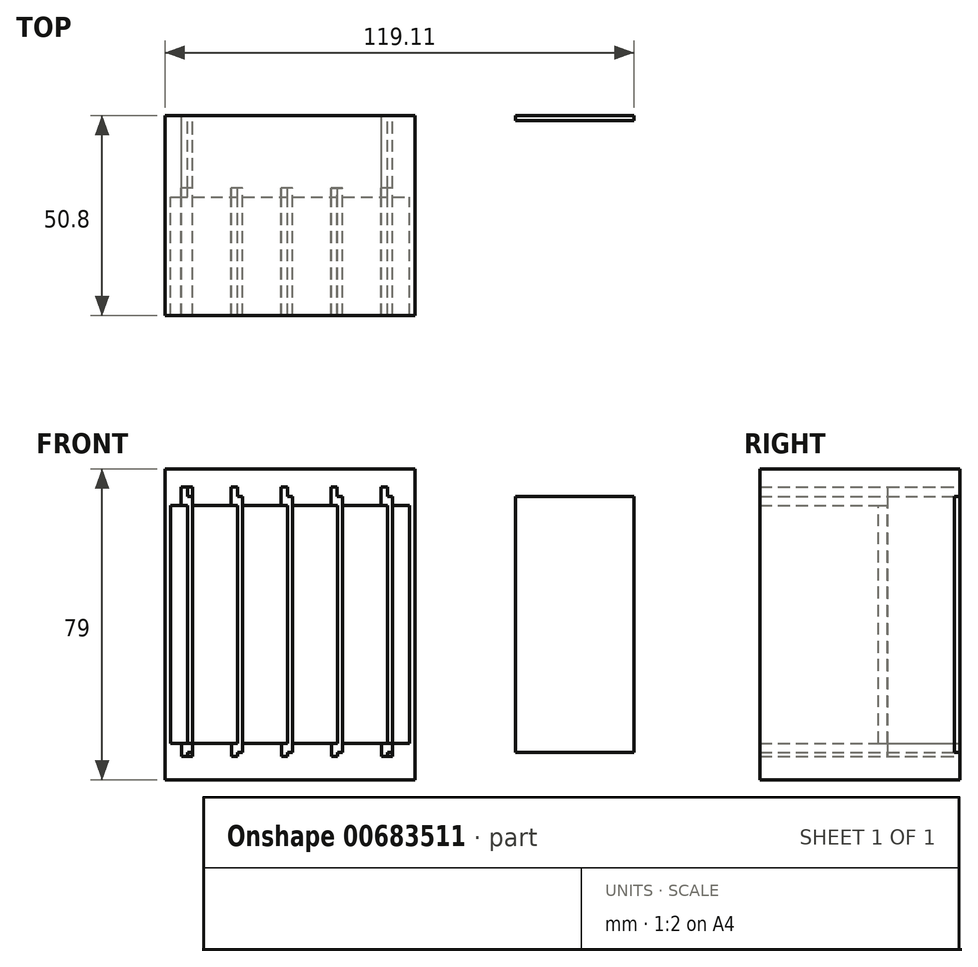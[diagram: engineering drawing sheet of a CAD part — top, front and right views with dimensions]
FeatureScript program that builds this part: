
annotation { "Feature Type Name" : "Feature", "Feature Type Description" : "" }
export const myFeature = defineFeature(function(context is Context, id is Id, definition is map)
    precondition{}
    {
        {
            var Q0;
            Q0=qCreatedBy(makeId("Front.planeOp"),FACE);
            var sketch = newSketch(context, id + "F0", { "sketchPlane" : qUnion([Q0])});
            skPoint(sketch, "E0.middle", {"position": v(-26.63, 1.14) * mm});
            skPoint(sketch, "E0.middle.positionSnap0", {"position": v(-32.98, 1.14) * mm});
            skPoint(sketch, "E0.centerSnap0", {"position": v(-32.98, 1.14) * mm});
            skLineSegment(sketch, "E1", {"start": v(30.52, 31.34) * mm, "end": v(30.52, -30.2) * mm});
            skPoint(sketch, "E2.middle", {"position": v(-13.93, 0) * mm});
            skPoint(sketch, "E3.middle", {"position": v(-1.23, 0) * mm});
            skPoint(sketch, "E4.middle", {"position": v(11.47, 0) * mm});
            skPoint(sketch, "E5.MirrorP", {"position": v(-61.95, 0) * mm});
            skLineSegment(sketch, "E6.MirrorCS", {"start": v(29.13, 32.48) * mm, "end": v(29.13, -30.2) * mm});
            skLineSegment(sketch, "E7.top", {"start": v(23.5, 31.34) * mm, "end": v(24.83, 31.34) * mm});
            skLineSegment(sketch, "E7.left", {"start": v(23.5, -30.2) * mm, "end": v(23.5, 31.34) * mm});
            skLineSegment(sketch, "E7.right", {"start": v(24.83, -30.2) * mm, "end": v(24.83, 31.34) * mm});
            skLineSegment(sketch, "E8.top", {"start": v(10.8, 31.34) * mm, "end": v(12.13, 31.34) * mm});
            skLineSegment(sketch, "E8.left", {"start": v(10.8, -30.2) * mm, "end": v(10.8, 31.34) * mm});
            skLineSegment(sketch, "E8.right", {"start": v(12.13, -30.2) * mm, "end": v(12.13, 31.34) * mm});
            skLineSegment(sketch, "E9.top", {"start": v(-1.9, 31.34) * mm, "end": v(-0.57, 31.34) * mm});
            skLineSegment(sketch, "E9.left", {"start": v(-1.9, -30.2) * mm, "end": v(-1.9, 31.34) * mm});
            skLineSegment(sketch, "E9.right", {"start": v(-0.57, -30.2) * mm, "end": v(-0.57, 31.34) * mm});
            skLineSegment(sketch, "E10.top", {"start": v(-14.6, 31.34) * mm, "end": v(-13.27, 31.34) * mm});
            skLineSegment(sketch, "E10.left", {"start": v(-14.6, -30.2) * mm, "end": v(-14.6, 31.34) * mm});
            skLineSegment(sketch, "E10.right", {"start": v(-13.27, -30.2) * mm, "end": v(-13.27, 31.34) * mm});
            skLineSegment(sketch, "E11.top", {"start": v(-27.3, 31.34) * mm, "end": v(-25.97, 31.34) * mm});
            skLineSegment(sketch, "E11.left", {"start": v(-27.3, -30.2) * mm, "end": v(-27.3, 31.34) * mm});
            skLineSegment(sketch, "E11.right", {"start": v(-25.97, -30.2) * mm, "end": v(-25.97, 31.34) * mm});
            skLineSegment(sketch, "E12.right", {"start": v(-32.98, 39.5) * mm, "end": v(-32.98, 30.2) * mm});
            skLineSegment(sketch, "E13.bottom", {"start": v(-32.98, 39.5) * mm, "end": v(-20.28, 39.5) * mm});
            skLineSegment(sketch, "E13.top", {"start": v(-32.98, 30.2) * mm, "end": v(-20.28, 30.2) * mm});
            skLineSegment(sketch, "E13.right", {"start": v(-20.28, 39.5) * mm, "end": v(-20.28, 30.2) * mm});
            skLineSegment(sketch, "E14.top", {"start": v(-25.97, 30.2) * mm, "end": v(-27.3, 30.2) * mm});
            skPoint(sketch, "E14.middle.positionSnap1", {"position": v(-26.63, 30.2) * mm});
            skPoint(sketch, "E14.centerSnap1", {"position": v(-26.63, 30.2) * mm});
            skLineSegment(sketch, "E15.bottom", {"start": v(-20.28, 39.5) * mm, "end": v(-7.58, 39.5) * mm});
            skLineSegment(sketch, "E15.top", {"start": v(-20.28, 30.2) * mm, "end": v(-7.58, 30.2) * mm});
            skLineSegment(sketch, "E15.right", {"start": v(-7.58, 39.5) * mm, "end": v(-7.58, 30.2) * mm});
            skLineSegment(sketch, "E16.bottom", {"start": v(-7.58, 39.5) * mm, "end": v(5.12, 39.5) * mm});
            skLineSegment(sketch, "E16.top", {"start": v(-7.58, 30.2) * mm, "end": v(5.12, 30.2) * mm});
            skLineSegment(sketch, "E16.right", {"start": v(5.12, 39.5) * mm, "end": v(5.12, 30.2) * mm});
            skLineSegment(sketch, "E17.bottom", {"start": v(5.12, 39.5) * mm, "end": v(17.82, 39.5) * mm});
            skLineSegment(sketch, "E17.top", {"start": v(5.12, 30.2) * mm, "end": v(17.82, 30.2) * mm});
            skLineSegment(sketch, "E17.right", {"start": v(17.82, 39.5) * mm, "end": v(17.82, 30.2) * mm});
            skLineSegment(sketch, "E18.bottom", {"start": v(17.82, 39.5) * mm, "end": v(30.52, 39.5) * mm});
            skLineSegment(sketch, "E18.top", {"start": v(17.82, 30.2) * mm, "end": v(30.52, 30.2) * mm});
            skLineSegment(sketch, "E18.right", {"start": v(30.52, 39.5) * mm, "end": v(30.52, 30.2) * mm});
            skLineSegment(sketch, "E19.top", {"start": v(-13.27, 30.2) * mm, "end": v(-14.6, 30.2) * mm});
            skPoint(sketch, "E19.middle.positionSnap0", {"position": v(-13.93, 30.2) * mm});
            skPoint(sketch, "E19.centerSnap0", {"position": v(-13.93, 30.2) * mm});
            skLineSegment(sketch, "E20.top", {"start": v(-0.57, 30.2) * mm, "end": v(-1.9, 30.2) * mm});
            skPoint(sketch, "E20.middle.positionSnap0", {"position": v(-1.23, 30.2) * mm});
            skLineSegment(sketch, "E21.top", {"start": v(12.13, 30.2) * mm, "end": v(10.8, 30.2) * mm});
            skPoint(sketch, "E21.middle.positionSnap0", {"position": v(11.47, 30.2) * mm});
            skPoint(sketch, "E21.centerSnap0", {"position": v(11.47, 30.2) * mm});
            skLineSegment(sketch, "E22.top", {"start": v(24.83, 30.2) * mm, "end": v(23.5, 30.2) * mm});
            skPoint(sketch, "E22.middle.positionSnap0", {"position": v(24.17, 30.2) * mm});
            skPoint(sketch, "E22.centerSnap0", {"position": v(24.17, 30.2) * mm});
            skLineSegment(sketch, "E23.bottom", {"start": v(-25.97, 34.9) * mm, "end": v(-28.95, 34.9) * mm});
            skLineSegment(sketch, "E23.top", {"start": v(-25.97, 30.2) * mm, "end": v(-28.95, 30.2) * mm});
            skLineSegment(sketch, "E23.left", {"start": v(-25.97, 34.9) * mm, "end": v(-25.97, 30.2) * mm});
            skLineSegment(sketch, "E23.right", {"start": v(-28.95, 34.9) * mm, "end": v(-28.95, 30.2) * mm});
            skLineSegment(sketch, "E24.bottom", {"start": v(-27.3, 34.9) * mm, "end": v(-25.97, 34.9) * mm});
            skLineSegment(sketch, "E24.top", {"start": v(-27.3, 32.5) * mm, "end": v(-25.97, 32.5) * mm});
            skLineSegment(sketch, "E24.left", {"start": v(-27.3, 34.9) * mm, "end": v(-27.3, 32.5) * mm});
            skLineSegment(sketch, "E24.right", {"start": v(-25.97, 34.9) * mm, "end": v(-25.97, 32.5) * mm});
            skLineSegment(sketch, "E25.MirrorCS", {"start": v(-14.6, 30.2) * mm, "end": v(-13.27, 30.2) * mm});
            skLineSegment(sketch, "E26.bottom", {"start": v(-13.27, 34.9) * mm, "end": v(-16.25, 34.9) * mm});
            skLineSegment(sketch, "E26.top", {"start": v(-13.27, 30.2) * mm, "end": v(-16.25, 30.2) * mm});
            skLineSegment(sketch, "E26.left", {"start": v(-13.27, 34.9) * mm, "end": v(-13.27, 30.2) * mm});
            skLineSegment(sketch, "E26.right", {"start": v(-16.25, 34.9) * mm, "end": v(-16.25, 30.2) * mm});
            skLineSegment(sketch, "E27.top", {"start": v(-14.6, 32.5) * mm, "end": v(-13.27, 32.5) * mm});
            skLineSegment(sketch, "E28.MirrorCS", {"start": v(-14.6, 34.9) * mm, "end": v(-14.6, 32.5) * mm});
            skLineSegment(sketch, "E29.bottom", {"start": v(-0.57, 34.9) * mm, "end": v(-3.55, 34.9) * mm});
            skLineSegment(sketch, "E29.top", {"start": v(-0.57, 30.2) * mm, "end": v(-3.55, 30.2) * mm});
            skLineSegment(sketch, "E29.left", {"start": v(-0.57, 34.9) * mm, "end": v(-0.57, 30.2) * mm});
            skLineSegment(sketch, "E29.right", {"start": v(-3.55, 34.9) * mm, "end": v(-3.55, 30.2) * mm});
            skLineSegment(sketch, "E30.top", {"start": v(-1.9, 32.5) * mm, "end": v(-0.57, 32.5) * mm});
            skLineSegment(sketch, "E31.MirrorCS", {"start": v(-1.9, 34.9) * mm, "end": v(-1.9, 32.5) * mm});
            skLineSegment(sketch, "E32.bottom", {"start": v(12.13, 34.9) * mm, "end": v(9.15, 34.9) * mm});
            skLineSegment(sketch, "E32.top", {"start": v(12.13, 30.2) * mm, "end": v(9.15, 30.2) * mm});
            skLineSegment(sketch, "E32.left", {"start": v(12.13, 34.9) * mm, "end": v(12.13, 30.2) * mm});
            skLineSegment(sketch, "E32.right", {"start": v(9.15, 34.9) * mm, "end": v(9.15, 30.2) * mm});
            skLineSegment(sketch, "E33.top", {"start": v(10.76, 32.5) * mm, "end": v(12.13, 32.5) * mm});
            skLineSegment(sketch, "E34.MirrorCS", {"start": v(10.76, 34.9) * mm, "end": v(10.76, 32.5) * mm});
            skLineSegment(sketch, "E35.bottom", {"start": v(24.83, 34.9) * mm, "end": v(21.85, 34.9) * mm});
            skLineSegment(sketch, "E35.top", {"start": v(24.83, 30.2) * mm, "end": v(21.85, 30.2) * mm});
            skLineSegment(sketch, "E35.left", {"start": v(24.83, 34.9) * mm, "end": v(24.83, 30.2) * mm});
            skLineSegment(sketch, "E35.right", {"start": v(21.85, 34.9) * mm, "end": v(21.85, 30.2) * mm});
            skLineSegment(sketch, "E36.top", {"start": v(23.5, 32.5) * mm, "end": v(24.83, 32.5) * mm});
            skLineSegment(sketch, "E37.MirrorCS", {"start": v(23.5, 34.9) * mm, "end": v(23.5, 32.5) * mm});
            skLineSegment(sketch, "E38.top", {"start": v(-32.98, -30.2) * mm, "end": v(31.98, -30.2) * mm});
            skLineSegment(sketch, "E39.bottom", {"start": v(-32.98, -30.2) * mm, "end": v(30.52, -30.2) * mm});
            skLineSegment(sketch, "E39.top", {"start": v(-32.98, -39.5) * mm, "end": v(30.52, -39.5) * mm});
            skLineSegment(sketch, "E39.left", {"start": v(-32.98, -30.2) * mm, "end": v(-32.98, -39.5) * mm});
            skLineSegment(sketch, "E39.right", {"start": v(30.52, -30.2) * mm, "end": v(30.52, -39.5) * mm});
            skLineSegment(sketch, "E40.bottom", {"start": v(-32.98, 30.2) * mm, "end": v(-31.6, 30.2) * mm});
            skLineSegment(sketch, "E40.top", {"start": v(-32.98, -30.2) * mm, "end": v(-31.6, -30.2) * mm});
            skLineSegment(sketch, "E40.left", {"start": v(-32.98, 30.2) * mm, "end": v(-32.98, -30.2) * mm});
            skLineSegment(sketch, "E40.right", {"start": v(-31.6, 30.2) * mm, "end": v(-31.6, -30.2) * mm});
            skLineSegment(sketch, "E41.bottom", {"start": v(30.52, -39.5) * mm, "end": v(-32.98, -39.5) * mm});
            skLineSegment(sketch, "E42.left", {"start": v(30.52, -39.5) * mm, "end": v(30.52, -30.2) * mm});
            skLineSegment(sketch, "E42.right", {"start": v(-32.98, -39.5) * mm, "end": v(-32.98, -30.2) * mm});
            skLineSegment(sketch, "E43.bottom", {"start": v(-25.97, -30.2) * mm, "end": v(-27.3, -30.2) * mm});
            skLineSegment(sketch, "E44.bottom", {"start": v(-13.27, -30.2) * mm, "end": v(-14.6, -30.2) * mm});
            skLineSegment(sketch, "E45.bottom", {"start": v(-0.57, -30.2) * mm, "end": v(-1.9, -30.2) * mm});
            skLineSegment(sketch, "E46.bottom", {"start": v(12.13, -30.2) * mm, "end": v(10.8, -30.2) * mm});
            skLineSegment(sketch, "E47.bottom", {"start": v(24.83, -30.2) * mm, "end": v(23.5, -30.2) * mm});
            skLineSegment(sketch, "E48.bottom", {"start": v(-25.97, -30.2) * mm, "end": v(-28.75, -30.2) * mm});
            skLineSegment(sketch, "E48.top", {"start": v(-25.97, -33.55) * mm, "end": v(-28.75, -33.55) * mm});
            skLineSegment(sketch, "E48.left", {"start": v(-25.97, -30.2) * mm, "end": v(-25.97, -33.55) * mm});
            skLineSegment(sketch, "E48.right", {"start": v(-28.75, -30.2) * mm, "end": v(-28.75, -33.55) * mm});
            skLineSegment(sketch, "E49.bottom", {"start": v(-25.97, -33.55) * mm, "end": v(-27.3, -33.55) * mm});
            skLineSegment(sketch, "E49.top", {"start": v(-25.97, -32.5) * mm, "end": v(-27.3, -32.5) * mm});
            skLineSegment(sketch, "E49.left", {"start": v(-25.97, -33.55) * mm, "end": v(-25.97, -32.5) * mm});
            skLineSegment(sketch, "E49.right", {"start": v(-27.3, -33.55) * mm, "end": v(-27.3, -32.5) * mm});
            skLineSegment(sketch, "E50.bottom", {"start": v(-13.27, -30.2) * mm, "end": v(-16.05, -30.2) * mm});
            skLineSegment(sketch, "E50.top", {"start": v(-13.27, -33.55) * mm, "end": v(-16.05, -33.55) * mm});
            skLineSegment(sketch, "E50.left", {"start": v(-13.27, -30.2) * mm, "end": v(-13.27, -33.55) * mm});
            skLineSegment(sketch, "E50.right", {"start": v(-16.05, -30.2) * mm, "end": v(-16.05, -33.55) * mm});
            skLineSegment(sketch, "E51.top", {"start": v(-13.27, -32.5) * mm, "end": v(-14.6, -32.5) * mm});
            skLineSegment(sketch, "E51.right", {"start": v(-14.6, -33.55) * mm, "end": v(-14.6, -32.5) * mm});
            skLineSegment(sketch, "E52.bottom", {"start": v(-0.57, -30.2) * mm, "end": v(-3.35, -30.2) * mm});
            skLineSegment(sketch, "E52.top", {"start": v(-0.57, -33.55) * mm, "end": v(-3.35, -33.55) * mm});
            skLineSegment(sketch, "E52.left", {"start": v(-0.57, -30.2) * mm, "end": v(-0.57, -33.55) * mm});
            skLineSegment(sketch, "E52.right", {"start": v(-3.35, -30.2) * mm, "end": v(-3.35, -33.55) * mm});
            skLineSegment(sketch, "E53.top", {"start": v(-0.57, -32.5) * mm, "end": v(-1.9, -32.5) * mm});
            skLineSegment(sketch, "E53.right", {"start": v(-1.9, -33.55) * mm, "end": v(-1.9, -32.5) * mm});
            skLineSegment(sketch, "E54.bottom", {"start": v(12.13, -30.2) * mm, "end": v(9.35, -30.2) * mm});
            skLineSegment(sketch, "E54.top", {"start": v(12.13, -33.55) * mm, "end": v(9.35, -33.55) * mm});
            skLineSegment(sketch, "E54.left", {"start": v(12.13, -30.2) * mm, "end": v(12.13, -33.55) * mm});
            skLineSegment(sketch, "E54.right", {"start": v(9.35, -30.2) * mm, "end": v(9.35, -33.55) * mm});
            skLineSegment(sketch, "E55.top", {"start": v(12.13, -32.5) * mm, "end": v(10.8, -32.5) * mm});
            skLineSegment(sketch, "E55.right", {"start": v(10.8, -33.55) * mm, "end": v(10.8, -32.5) * mm});
            skLineSegment(sketch, "E56.bottom", {"start": v(24.83, -30.2) * mm, "end": v(22.05, -30.2) * mm});
            skLineSegment(sketch, "E56.top", {"start": v(24.83, -33.55) * mm, "end": v(22.05, -33.55) * mm});
            skLineSegment(sketch, "E56.left", {"start": v(24.83, -30.2) * mm, "end": v(24.83, -33.55) * mm});
            skLineSegment(sketch, "E56.right", {"start": v(22.05, -30.2) * mm, "end": v(22.05, -33.55) * mm});
            skLineSegment(sketch, "E57.bottom", {"start": v(24.83, -33.55) * mm, "end": v(23.5, -33.55) * mm});
            skLineSegment(sketch, "E57.top", {"start": v(24.83, -32.5) * mm, "end": v(23.5, -32.5) * mm});
            skLineSegment(sketch, "E57.left", {"start": v(24.83, -33.55) * mm, "end": v(24.83, -32.5) * mm});
            skLineSegment(sketch, "E57.right", {"start": v(23.5, -33.55) * mm, "end": v(23.5, -32.5) * mm});
            skLineSegment(sketch, "E58.bottom", {"start": v(23.5, -30.2) * mm, "end": v(24.83, -30.2) * mm});
            skLineSegment(sketch, "E59.bottom", {"start": v(10.8, -30.2) * mm, "end": v(12.13, -30.2) * mm});
            skLineSegment(sketch, "E60.bottom", {"start": v(-1.9, -30.2) * mm, "end": v(-0.57, -30.2) * mm});
            skLineSegment(sketch, "E61.bottom", {"start": v(-14.6, -30.2) * mm, "end": v(-13.27, -30.2) * mm});
            skLineSegment(sketch, "E62.bottom", {"start": v(-27.3, -30.2) * mm, "end": v(-25.97, -30.2) * mm});
            skSolve(sketch);
        }
        {
            var Q0;
            Q0=qCreatedBy(makeId("Front.planeOp"),FACE);
            var sketch = newSketch(context, id + "F1", { "sketchPlane" : qUnion([Q0])});
            skLineSegment(sketch, "E63.bottom", {"start": v(86.13, -32.5) * mm, "end": v(56, -32.5) * mm});
            skLineSegment(sketch, "E63.top", {"start": v(86.13, 32.5) * mm, "end": v(56, 32.5) * mm});
            skLineSegment(sketch, "E63.left", {"start": v(86.13, -32.5) * mm, "end": v(86.13, 32.5) * mm});
            skLineSegment(sketch, "E63.right", {"start": v(56, -32.5) * mm, "end": v(56, 32.5) * mm});
            skPoint(sketch, "E63.middle", {"position": v(71.06, 0) * mm});
            skSolve(sketch);
        }
        {
            var Q0;
            Q0=qSketchRegion(id+"F1",true);
            extrude(context, id + "F2", {"entities" : qUnion([Q0]), "depth" : 1.33 * mm, "offsetDistance" : 25.4 * mm});
        }
        {
            var Q0;
            Q0=qSketchRegion(id+"F0",true);
            var Q1;
            {var subQ0=sQuery(id+"F0.wireOp",EDGE,"E24.bottom");Q1=makeQuery(id+"F0.imprint","IMPRINT",FACE,{"disambiguationData":[TD([[makeQuery(id+"F0.imprint","IMPRINT",EDGE,{"derivedFrom":subQ0}),-1.0]])]});}
            var Q2;
            {var subQ4=sQuery(id+"F0.wireOp",EDGE,"E27.top");Q2=makeQuery(id+"F0.imprint","IMPRINT",FACE,{"disambiguationData":[TD([[makeQuery(id+"F0.imprint","IMPRINT",EDGE,{"derivedFrom":subQ4}),1.0]])]});}
            var Q3;
            {var subQ4=sQuery(id+"F0.wireOp",EDGE,"E30.top");Q3=makeQuery(id+"F0.imprint","IMPRINT",FACE,{"disambiguationData":[TD([[makeQuery(id+"F0.imprint","IMPRINT",EDGE,{"derivedFrom":subQ4}),1.0]])]});}
            var Q4;
            {var subQ4=sQuery(id+"F0.wireOp",EDGE,"E33.top");Q4=makeQuery(id+"F0.imprint","IMPRINT",FACE,{"disambiguationData":[TD([[makeQuery(id+"F0.imprint","IMPRINT",EDGE,{"derivedFrom":subQ4}),1.0]])]});}
            var Q5;
            {var subQ4=sQuery(id+"F0.wireOp",EDGE,"E36.top");Q5=makeQuery(id+"F0.imprint","IMPRINT",FACE,{"disambiguationData":[TD([[makeQuery(id+"F0.imprint","IMPRINT",EDGE,{"derivedFrom":subQ4}),1.0]])]});}
            var Q6;
            Q6=makeQuery(id+"F0.imprint","IMPRINT",FACE,{"disambiguationData":[TD([[makeQuery(id+"F0.imprint","IMPRINT",EDGE,{"derivedFrom":sQuery(id+"F0.wireOp",EDGE,"E57.bottom")}),-1.0]])]});
            var Q7;
            {var subQ4=sQuery(id+"F0.wireOp",EDGE,"E55.top");Q7=makeQuery(id+"F0.imprint","IMPRINT",FACE,{"disambiguationData":[TD([[makeQuery(id+"F0.imprint","IMPRINT",EDGE,{"derivedFrom":subQ4}),1.0]])]});}
            var Q8;
            {var subQ4=sQuery(id+"F0.wireOp",EDGE,"E53.top");Q8=makeQuery(id+"F0.imprint","IMPRINT",FACE,{"disambiguationData":[TD([[makeQuery(id+"F0.imprint","IMPRINT",EDGE,{"derivedFrom":subQ4}),1.0]])]});}
            var Q9;
            {var subQ4=sQuery(id+"F0.wireOp",EDGE,"E51.top");Q9=makeQuery(id+"F0.imprint","IMPRINT",FACE,{"disambiguationData":[TD([[makeQuery(id+"F0.imprint","IMPRINT",EDGE,{"derivedFrom":subQ4}),1.0]])]});}
            var Q10;
            Q10=makeQuery(id+"F0.imprint","IMPRINT",FACE,{"disambiguationData":[TD([[makeQuery(id+"F0.imprint","IMPRINT",EDGE,{"derivedFrom":sQuery(id+"F0.wireOp",EDGE,"E49.bottom")}),-1.0]])]});
            extrude(context, id + "F3", {"entities" : qUnion([Q0, Q1, Q2, Q3, Q4, Q5, Q6, Q7, Q8, Q9, Q10]), "depth" : 50.8 * mm, "offsetDistance" : 25.4 * mm});
        }
        {
            var Q0;
            {var subQ0=sQuery(id+"F0.wireOp",EDGE,"E40.right");Q0=makeQuery(id+"F0.imprint","IMPRINT",FACE,{"disambiguationData":[TD([[makeQuery(id+"F0.imprint","IMPRINT",EDGE,{"derivedFrom":subQ0}),1.0]])]});}
            var Q1;
            {var subQ5=sQuery(id+"F0.wireOp",EDGE,"E11.right");Q1=makeQuery(id+"F0.imprint","IMPRINT",FACE,{"disambiguationData":[TD([[makeQuery(id+"F0.imprint","IMPRINT",EDGE,{"derivedFrom":subQ5}),-1.0]])]});}
            var Q2;
            {var subQ1=sQuery(id+"F0.wireOp",EDGE,"E10.right");Q2=makeQuery(id+"F0.imprint","IMPRINT",FACE,{"disambiguationData":[TD([[makeQuery(id+"F0.imprint","IMPRINT",EDGE,{"derivedFrom":subQ1}),-1.0]])]});}
            var Q3;
            {var subQ5=sQuery(id+"F0.wireOp",EDGE,"E9.right");Q3=makeQuery(id+"F0.imprint","IMPRINT",FACE,{"disambiguationData":[TD([[makeQuery(id+"F0.imprint","IMPRINT",EDGE,{"derivedFrom":subQ5}),-1.0]])]});}
            var Q4;
            {var subQ1=sQuery(id+"F0.wireOp",EDGE,"E8.right");Q4=makeQuery(id+"F0.imprint","IMPRINT",FACE,{"disambiguationData":[TD([[makeQuery(id+"F0.imprint","IMPRINT",EDGE,{"derivedFrom":subQ1}),-1.0]])]});}
            var Q5;
            {var subQ5=sQuery(id+"F0.wireOp",EDGE,"E7.right");Q5=makeQuery(id+"F0.imprint","IMPRINT",FACE,{"disambiguationData":[TD([[makeQuery(id+"F0.imprint","IMPRINT",EDGE,{"derivedFrom":subQ5}),-1.0]])]});}
            extrude(context, id + "F4", {"entities" : qUnion([Q0, Q1, Q2, Q3, Q4, Q5]), "operationType" : NewBodyOperationType.ADD, "depth" : 20.66 * mm, "offsetDistance" : 25.4 * mm});
        }
        {
            var Q0;
            {var subQ4=sQuery(id+"F0.wireOp",EDGE,"E11.top");Q0=makeQuery(id+"F0.imprint","IMPRINT",FACE,{"disambiguationData":[TD([[makeQuery(id+"F0.imprint","IMPRINT",EDGE,{"derivedFrom":subQ4}),1.0]])]});}
            var Q1;
            {var subQ0=sQuery(id+"F0.wireOp",EDGE,"E11.top");Q1=makeQuery(id+"F0.imprint","IMPRINT",FACE,{"disambiguationData":[TD([[makeQuery(id+"F0.imprint","IMPRINT",EDGE,{"derivedFrom":subQ0}),-1.0]])]});}
            var Q2;
            {var subQ5=sQuery(id+"F0.wireOp",EDGE,"E11.right");Q2=makeQuery(id+"F0.imprint","IMPRINT",FACE,{"disambiguationData":[TD([[makeQuery(id+"F0.imprint","IMPRINT",EDGE,{"derivedFrom":subQ5}),1.0]])]});}
            var Q3;
            Q3=makeQuery(id+"F0.imprint","IMPRINT",FACE,{"disambiguationData":[TD([[makeQuery(id+"F0.imprint","IMPRINT",EDGE,{"derivedFrom":sQuery(id+"F0.wireOp",EDGE,"E48.top")}),-1.0]])]});
            var Q4;
            {var subQ6=sQuery(id+"F0.wireOp",EDGE,"E10.top");Q4=makeQuery(id+"F0.imprint","IMPRINT",FACE,{"disambiguationData":[TD([[makeQuery(id+"F0.imprint","IMPRINT",EDGE,{"derivedFrom":subQ6}),1.0]])]});}
            var Q5;
            {var subQ0=sQuery(id+"F0.wireOp",EDGE,"E10.top");Q5=makeQuery(id+"F0.imprint","IMPRINT",FACE,{"disambiguationData":[TD([[makeQuery(id+"F0.imprint","IMPRINT",EDGE,{"derivedFrom":subQ0}),-1.0]])]});}
            var Q6;
            {var subQ5=sQuery(id+"F0.wireOp",EDGE,"E10.right");Q6=makeQuery(id+"F0.imprint","IMPRINT",FACE,{"disambiguationData":[TD([[makeQuery(id+"F0.imprint","IMPRINT",EDGE,{"derivedFrom":subQ5}),1.0]])]});}
            var Q7;
            {var subQ1=sQuery(id+"F0.wireOp",EDGE,"E50.right");Q7=makeQuery(id+"F0.imprint","IMPRINT",FACE,{"disambiguationData":[TD([[makeQuery(id+"F0.imprint","IMPRINT",EDGE,{"derivedFrom":subQ1}),1.0]])]});}
            var Q8;
            {var subQ1=sQuery(id+"F0.wireOp",EDGE,"E52.right");Q8=makeQuery(id+"F0.imprint","IMPRINT",FACE,{"disambiguationData":[TD([[makeQuery(id+"F0.imprint","IMPRINT",EDGE,{"derivedFrom":subQ1}),1.0]])]});}
            var Q9;
            {var subQ5=sQuery(id+"F0.wireOp",EDGE,"E9.right");Q9=makeQuery(id+"F0.imprint","IMPRINT",FACE,{"disambiguationData":[TD([[makeQuery(id+"F0.imprint","IMPRINT",EDGE,{"derivedFrom":subQ5}),1.0]])]});}
            var Q10;
            {var subQ0=sQuery(id+"F0.wireOp",EDGE,"E9.top");Q10=makeQuery(id+"F0.imprint","IMPRINT",FACE,{"disambiguationData":[TD([[makeQuery(id+"F0.imprint","IMPRINT",EDGE,{"derivedFrom":subQ0}),-1.0]])]});}
            var Q11;
            {var subQ4=sQuery(id+"F0.wireOp",EDGE,"E9.top");Q11=makeQuery(id+"F0.imprint","IMPRINT",FACE,{"disambiguationData":[TD([[makeQuery(id+"F0.imprint","IMPRINT",EDGE,{"derivedFrom":subQ4}),1.0]])]});}
            var Q12;
            {var subQ6=sQuery(id+"F0.wireOp",EDGE,"E8.top");Q12=makeQuery(id+"F0.imprint","IMPRINT",FACE,{"disambiguationData":[TD([[makeQuery(id+"F0.imprint","IMPRINT",EDGE,{"derivedFrom":subQ6}),1.0]])]});}
            var Q13;
            {var subQ0=sQuery(id+"F0.wireOp",EDGE,"E8.top");Q13=makeQuery(id+"F0.imprint","IMPRINT",FACE,{"disambiguationData":[TD([[makeQuery(id+"F0.imprint","IMPRINT",EDGE,{"derivedFrom":subQ0}),-1.0]])]});}
            var Q14;
            {var subQ5=sQuery(id+"F0.wireOp",EDGE,"E8.right");Q14=makeQuery(id+"F0.imprint","IMPRINT",FACE,{"disambiguationData":[TD([[makeQuery(id+"F0.imprint","IMPRINT",EDGE,{"derivedFrom":subQ5}),1.0]])]});}
            var Q15;
            {var subQ1=sQuery(id+"F0.wireOp",EDGE,"E54.right");Q15=makeQuery(id+"F0.imprint","IMPRINT",FACE,{"disambiguationData":[TD([[makeQuery(id+"F0.imprint","IMPRINT",EDGE,{"derivedFrom":subQ1}),1.0]])]});}
            var Q16;
            {var subQ4=sQuery(id+"F0.wireOp",EDGE,"E7.top");Q16=makeQuery(id+"F0.imprint","IMPRINT",FACE,{"disambiguationData":[TD([[makeQuery(id+"F0.imprint","IMPRINT",EDGE,{"derivedFrom":subQ4}),1.0]])]});}
            var Q17;
            {var subQ0=sQuery(id+"F0.wireOp",EDGE,"E7.top");Q17=makeQuery(id+"F0.imprint","IMPRINT",FACE,{"disambiguationData":[TD([[makeQuery(id+"F0.imprint","IMPRINT",EDGE,{"derivedFrom":subQ0}),-1.0]])]});}
            var Q18;
            {var subQ5=sQuery(id+"F0.wireOp",EDGE,"E7.right");Q18=makeQuery(id+"F0.imprint","IMPRINT",FACE,{"disambiguationData":[TD([[makeQuery(id+"F0.imprint","IMPRINT",EDGE,{"derivedFrom":subQ5}),1.0]])]});}
            var Q19;
            Q19=makeQuery(id+"F0.imprint","IMPRINT",FACE,{"disambiguationData":[TD([[makeQuery(id+"F0.imprint","IMPRINT",EDGE,{"derivedFrom":sQuery(id+"F0.wireOp",EDGE,"E56.top")}),-1.0]])]});
            extrude(context, id + "F5", {"entities" : qUnion([Q0, Q1, Q2, Q3, Q4, Q5, Q6, Q7, Q8, Q9, Q10, Q11, Q12, Q13, Q14, Q15, Q16, Q17, Q18, Q19]), "operationType" : NewBodyOperationType.ADD, "depth" : 18.36 * mm, "offsetDistance" : 25.4 * mm});
        }
    });
